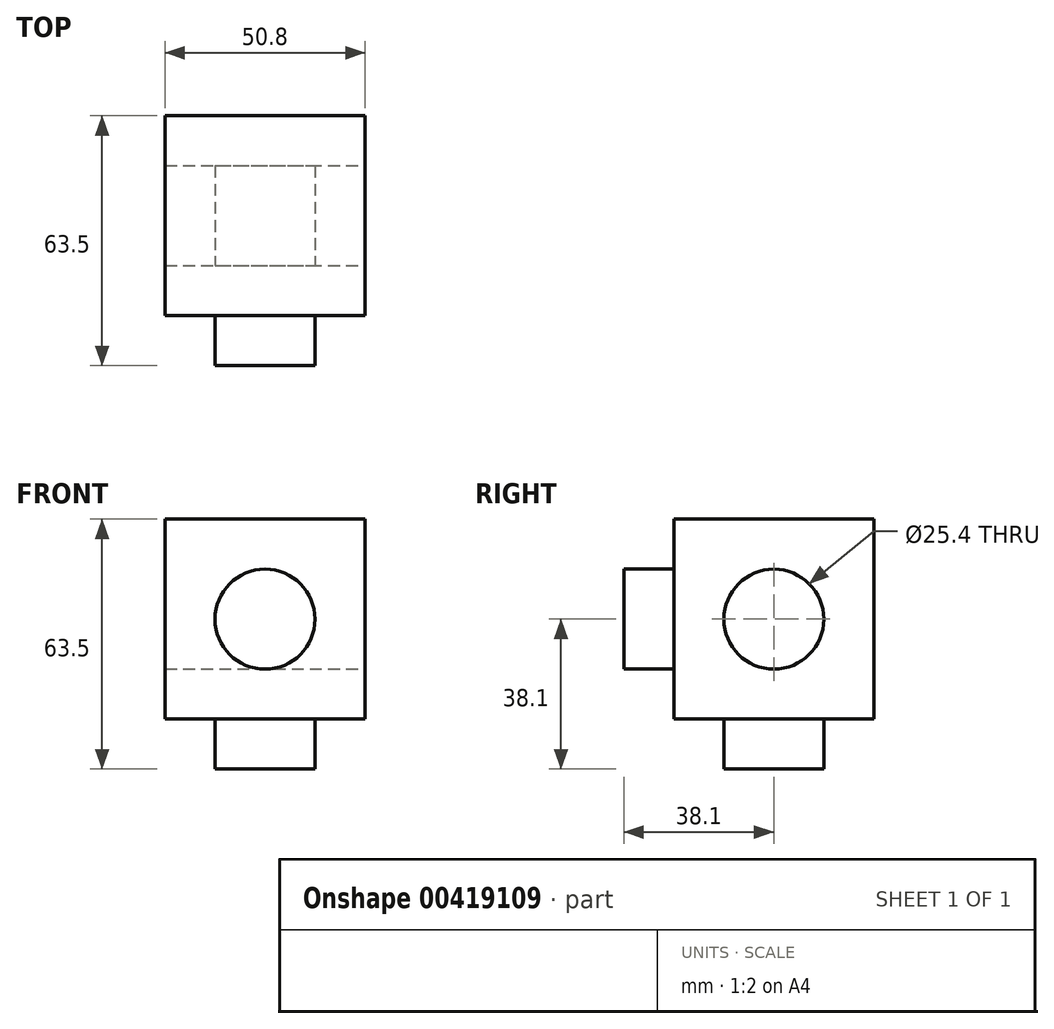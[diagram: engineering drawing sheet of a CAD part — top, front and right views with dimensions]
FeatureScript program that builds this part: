
annotation { "Feature Type Name" : "Feature", "Feature Type Description" : "" }
export const myFeature = defineFeature(function(context is Context, id is Id, definition is map)
    precondition{}
    {
        {
            var Q0;
            Q0=qCreatedBy(makeId("Front.planeOp"),FACE);
            var sketch = newSketch(context, id + "F0", { "sketchPlane" : qUnion([Q0])});
            skLineSegment(sketch, "E0.bottom", {"start": v(0, 0) * mm, "end": v(-50.8, 0) * mm});
            skLineSegment(sketch, "E0.top", {"start": v(0, 50.8) * mm, "end": v(-50.8, 50.8) * mm});
            skLineSegment(sketch, "E0.left", {"start": v(0, 0) * mm, "end": v(0, 50.8) * mm});
            skLineSegment(sketch, "E0.right", {"start": v(-50.8, 0) * mm, "end": v(-50.8, 50.8) * mm});
            skSolve(sketch);
        }
        {
            var Q0;
            Q0=makeQuery(id+"F0.imprint","IMPRINT",FACE,{"disambiguationData":[TD([[makeQuery(id+"F0.imprint","IMPRINT",EDGE,{"derivedFrom":sQuery(id+"F0.wireOp",EDGE,"E0.bottom")}),-1.0]])]});
            extrude(context, id + "F1", {"entities" : qUnion([Q0]), "depth" : 50.8 * mm});
        }
        {
            var Q0;
            Q0=makeQuery(id+"F1.opExtrude","CAP_FACE",FACE,{"disambiguationData":[OSD([sQuery(id+"F0.wireOp",EDGE,"E0.bottom"),sQuery(id+"F0.wireOp",EDGE,"E0.top"),sQuery(id+"F0.wireOp",EDGE,"E0.left"),sQuery(id+"F0.wireOp",EDGE,"E0.right")])],"isStart":false});
            var sketch = newSketch(context, id + "F2", { "sketchPlane" : qUnion([Q0])});
            skCircle(sketch, "E1", {"center": v(-25.4, 25.4) * mm, "radius": 12.7 * mm});
            skSolve(sketch);
        }
        {
            var Q0;
            Q0 = qSketchRegion(id + "F2", true);
            extrude(context, id + "F3", {"entities" : qUnion([Q0]), "operationType" : NewBodyOperationType.ADD, "depth" : 12.7 * mm});
        }
        {
            var Q0;
            Q0=makeQuery(id+"F1.opExtrude","SWEPT_FACE",FACE,{"disambiguationData":[OSD([sQuery(id+"F0.wireOp",EDGE,"E0.bottom")])]});
            var sketch = newSketch(context, id + "F4", { "sketchPlane" : qUnion([Q0])});
            skLineSegment(sketch, "E2.bottom", {"start": v(-38.1, 12.7) * mm, "end": v(-12.7, 12.7) * mm});
            skLineSegment(sketch, "E2.top", {"start": v(-38.1, 38.1) * mm, "end": v(-12.7, 38.1) * mm});
            skLineSegment(sketch, "E2.left", {"start": v(-38.1, 12.7) * mm, "end": v(-38.1, 38.1) * mm});
            skLineSegment(sketch, "E2.right", {"start": v(-12.7, 12.7) * mm, "end": v(-12.7, 38.1) * mm});
            skSolve(sketch);
        }
        {
            var Q0;
            Q0 = qSketchRegion(id + "F4", true);
            extrude(context, id + "F5", {"entities" : qUnion([Q0]), "operationType" : NewBodyOperationType.ADD, "depth" : 12.7 * mm});
        }
        {
            var Q0;
            Q0=makeQuery(id+"F1.opExtrude","SWEPT_FACE",FACE,{"disambiguationData":[OSD([sQuery(id+"F0.wireOp",EDGE,"E0.left")])]});
            var sketch = newSketch(context, id + "F6", { "sketchPlane" : qUnion([Q0])});
            skCircle(sketch, "E3", {"center": v(-25.4, 25.4) * mm, "radius": 12.7 * mm});
            skSolve(sketch);
        }
        {
            var Q0;
            Q0 = qSketchRegion(id + "F6", true);
            extrude(context, id + "F7", {"entities" : qUnion([Q0]), "operationType" : NewBodyOperationType.REMOVE, "oppositeDirection" : true, "depth" : 50.8 * mm});
        }
    });
